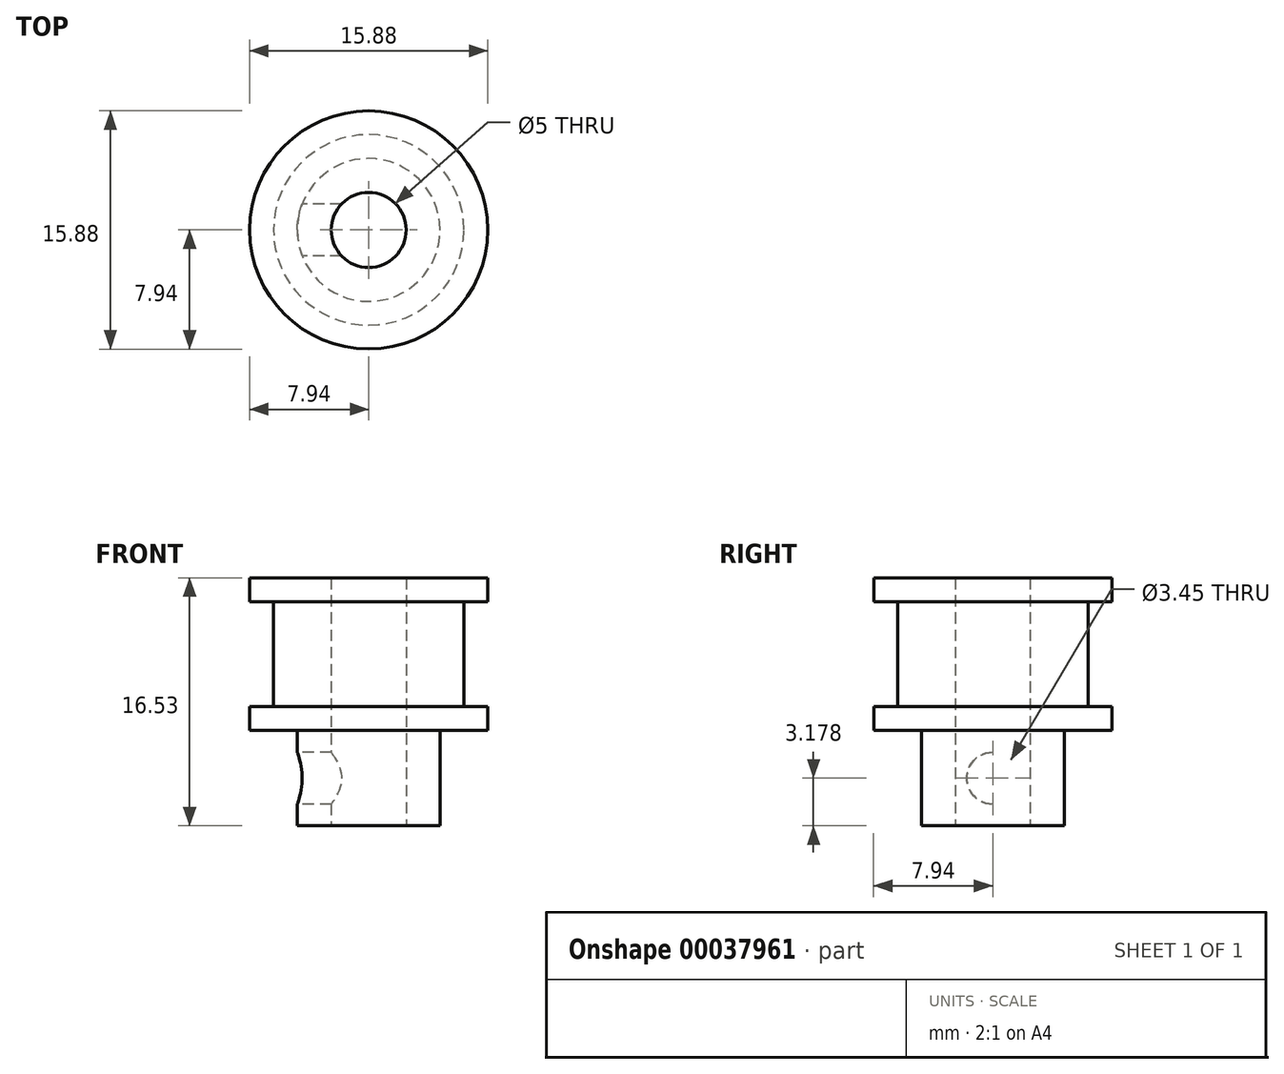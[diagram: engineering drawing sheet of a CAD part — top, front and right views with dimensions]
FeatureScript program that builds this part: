
annotation { "Feature Type Name" : "Feature", "Feature Type Description" : "" }
export const myFeature = defineFeature(function(context is Context, id is Id, definition is map)
    precondition{}
    {
        {
            var Q0;
            Q0=qCreatedBy(makeId("Top.planeOp"),FACE);
            var sketch = newSketch(context, id + "F0", { "sketchPlane" : qUnion([Q0])});
            skCircle(sketch, "E0", {"center": v(0, 0) * mm, "radius": 6.35 * mm});
            skSolve(sketch);
        }
        {
            var Q0;
            Q0=qSketchRegion(id+"F0",true);
            extrude(context, id + "F1", {"entities" : qUnion([Q0]), "depth" : 7 * mm});
        }
        {
            var Q0;
            Q0=makeQuery(id+"F1.opExtrude","CAP_FACE",FACE,{"disambiguationData":[OSD([sQuery(id+"F0.wireOp",EDGE,"E0")])],"isStart":false});
            var sketch = newSketch(context, id + "F2", { "sketchPlane" : qUnion([Q0])});
            skCircle(sketch, "E1", {"center": v(0, 0) * mm, "radius": 7.94 * mm});
            skSolve(sketch);
        }
        {
            var Q0;
            Q0=qSketchRegion(id+"F2",true);
            extrude(context, id + "F3", {"entities" : qUnion([Q0]), "operationType" : NewBodyOperationType.ADD, "depth" : 1.59 * mm});
        }
        {
            var Q0;
            Q0=makeQuery(id+"F1.opExtrude","CAP_FACE",FACE,{"disambiguationData":[OSD([sQuery(id+"F0.wireOp",EDGE,"E0")])],"isStart":true});
            var sketch = newSketch(context, id + "F4", { "sketchPlane" : qUnion([Q0])});
            skCircle(sketch, "E2", {"center": v(0, 0) * mm, "radius": 7.94 * mm});
            skSolve(sketch);
        }
        {
            var Q0;
            Q0=qSketchRegion(id+"F4",true);
            extrude(context, id + "F5", {"entities" : qUnion([Q0]), "operationType" : NewBodyOperationType.ADD, "depth" : 1.59 * mm});
        }
        {
            var Q0;
            Q0=makeQuery(id+"F5.opExtrude","CAP_FACE",FACE,{"disambiguationData":[OSD([sQuery(id+"F4.wireOp",EDGE,"E2")])],"isStart":false});
            var sketch = newSketch(context, id + "F6", { "sketchPlane" : qUnion([Q0])});
            skLineSegment(sketch, "E3.rect.bottom", {"start": v(-4.76, -4.76) * mm, "end": v(4.76, -4.76) * mm});
            skLineSegment(sketch, "E3.rect.top", {"start": v(-4.76, 4.76) * mm, "end": v(4.76, 4.76) * mm});
            skLineSegment(sketch, "E3.rect.left", {"start": v(-4.76, -4.76) * mm, "end": v(-4.76, 4.76) * mm});
            skLineSegment(sketch, "E3.rect.right", {"start": v(4.76, -4.76) * mm, "end": v(4.76, 4.76) * mm});
            skPoint(sketch, "E3.rect.middle", {"position": v(0, 0) * mm});
            skSolve(sketch);
        }
        {
            var Q0;
            Q0=qSketchRegion(id+"F6",true);
            extrude(context, id + "F7", {"entities" : qUnion([Q0]), "operationType" : NewBodyOperationType.ADD, "depth" : 6.35 * mm});
        }
        {
            var Q0;
            Q0=makeQuery(id+"F7.opExtrude","CAP_FACE",FACE,{"disambiguationData":[OSD([sQuery(id+"F6.wireOp",EDGE,"E3.rect.bottom"),sQuery(id+"F6.wireOp",EDGE,"E3.rect.top"),sQuery(id+"F6.wireOp",EDGE,"E3.rect.left"),sQuery(id+"F6.wireOp",EDGE,"E3.rect.right")])],"isStart":false});
            var sketch = newSketch(context, id + "F8", { "sketchPlane" : qUnion([Q0])});
            skCircle(sketch, "E4", {"center": v(0, 0) * mm, "radius": 2.5 * mm});
            skSolve(sketch);
        }
        {
            var Q0;
            Q0=qSketchRegion(id+"F8",true);
            var Q1;
            Q1=makeQuery(id+"F3.opExtrude","CAP_FACE",FACE,{"disambiguationData":[OSD([sQuery(id+"F2.wireOp",EDGE,"E1")])],"isStart":false});
            extrude(context, id + "F9", {"entities" : qUnion([Q0]), "operationType" : NewBodyOperationType.REMOVE, "endBound" : BoundingType.UP_TO_SURFACE, "oppositeDirection" : true, "endBoundEntityFace" : qUnion([Q1]), "depth" : 25.4 * mm});
        }
        {
            var Q0;
            Q0=makeQuery(id+"F7.opExtrude","SWEPT_FACE",FACE,{"disambiguationData":[OSD([sQuery(id+"F6.wireOp",EDGE,"E3.rect.left")])]});
            var sketch = newSketch(context, id + "F10", { "sketchPlane" : qUnion([Q0])});
            skLineSegment(sketch, "E5", {"start": v(0, -7.94) * mm, "end": v(0, -1.59) * mm});
            skCircle(sketch, "E6", {"center": v(0, -4.76) * mm, "radius": 1.73 * mm});
            skSolve(sketch);
        }
        {
            var Q0;
            Q0=qSketchRegion(id+"F10",true);
            var Q1;
            Q1=makeQuery(id+"F9.boolean.opBoolean","COPY",FACE,{"derivedFrom":makeQuery(id+"F9.opExtrude","SWEPT_FACE",FACE,{"disambiguationData":[OSD([sQuery(id+"F8.wireOp",EDGE,"E4")])]})});
            extrude(context, id + "F11", {"entities" : qUnion([Q0]), "operationType" : NewBodyOperationType.REMOVE, "endBound" : BoundingType.UP_TO_SURFACE, "oppositeDirection" : true, "endBoundEntityFace" : qUnion([Q1]), "depth" : 25.4 * mm});
        }
        {
            var Q0;
            Q0=makeQuery(id+"F7.opExtrude","SWEPT_EDGE",EDGE,{"disambiguationData":[OSD([sQuery(id+"F6.wireOp",EDGE,"E3.rect.top"),sQuery(id+"F6.wireOp",EDGE,"E3.rect.left")])]});
            var Q1;
            Q1=makeQuery(id+"F7.opExtrude","SWEPT_EDGE",EDGE,{"disambiguationData":[OSD([sQuery(id+"F6.wireOp",EDGE,"E3.rect.bottom"),sQuery(id+"F6.wireOp",EDGE,"E3.rect.left")])]});
            var Q2;
            Q2=makeQuery(id+"F7.opExtrude","SWEPT_EDGE",EDGE,{"disambiguationData":[OSD([sQuery(id+"F6.wireOp",EDGE,"E3.rect.bottom"),sQuery(id+"F6.wireOp",EDGE,"E3.rect.right")])]});
            var Q3;
            Q3=makeQuery(id+"F7.opExtrude","SWEPT_EDGE",EDGE,{"disambiguationData":[OSD([sQuery(id+"F6.wireOp",EDGE,"E3.rect.top"),sQuery(id+"F6.wireOp",EDGE,"E3.rect.right")])]});
            fillet(context, id + "F12", {"entities" : qUnion([Q0, Q1, Q2, Q3]), "radius" : 4.76 * mm, "allowEdgeOverflow" : false});
        }
    });
